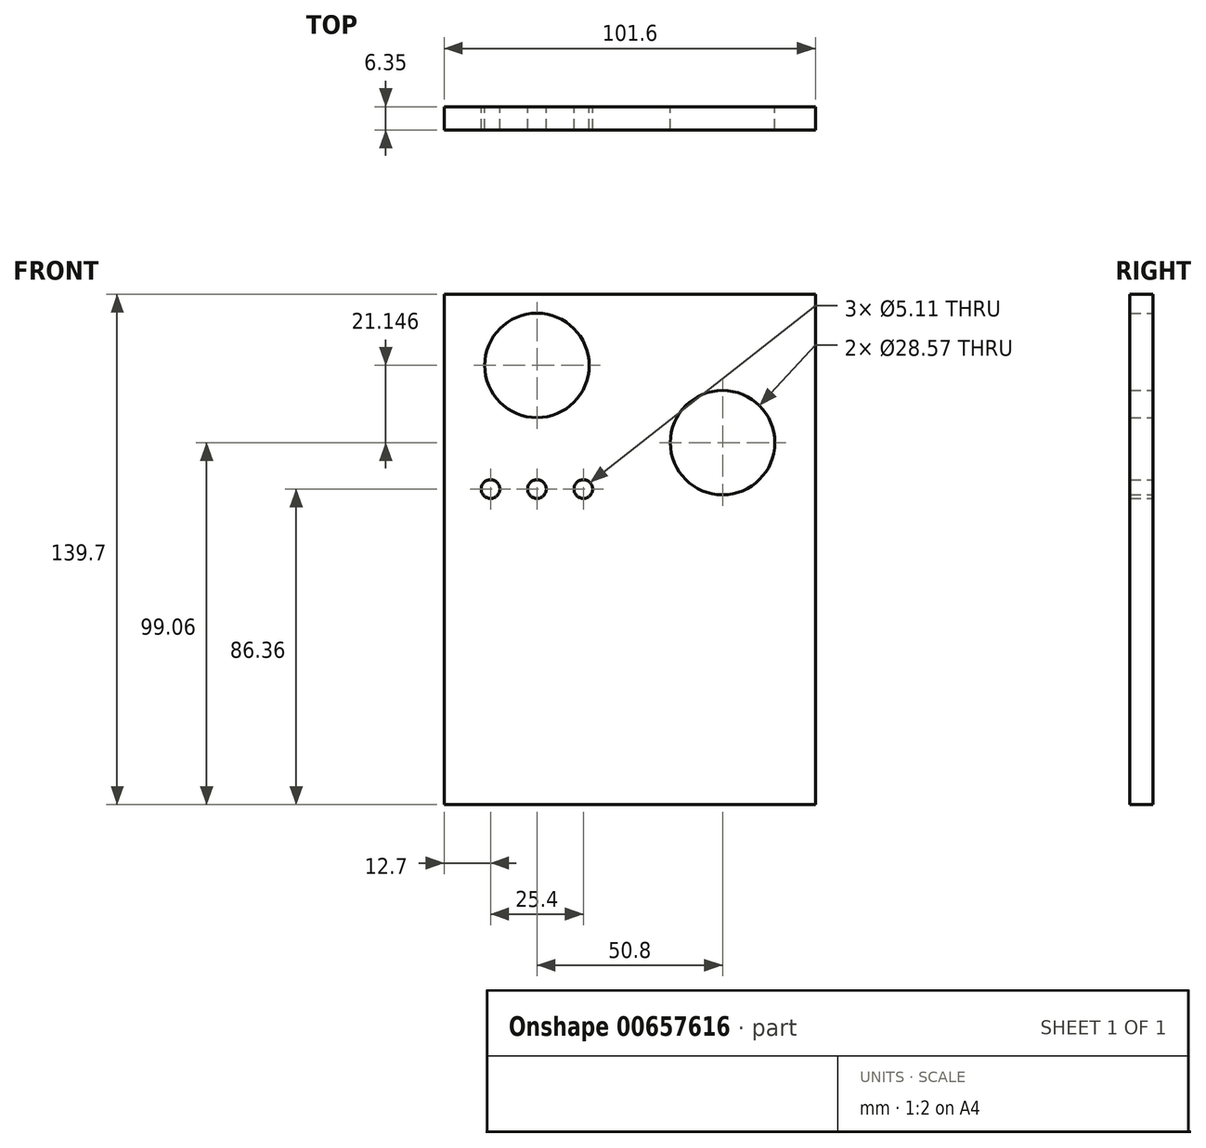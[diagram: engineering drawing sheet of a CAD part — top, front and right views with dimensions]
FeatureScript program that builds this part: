
annotation { "Feature Type Name" : "Feature", "Feature Type Description" : "" }
export const myFeature = defineFeature(function(context is Context, id is Id, definition is map)
    precondition{}
    {
        {
            var Q0;
            Q0=qCreatedBy(makeId("Front.planeOp"),FACE);
            var sketch = newSketch(context, id + "F0", { "sketchPlane" : qUnion([Q0])});
            skLineSegment(sketch, "E0.bottom", {"start": v(0, 0) * mm, "end": v(101.6, 0) * mm});
            skLineSegment(sketch, "E0.top", {"start": v(0, -139.7) * mm, "end": v(101.6, -139.7) * mm});
            skLineSegment(sketch, "E0.left", {"start": v(0, 0) * mm, "end": v(0, -139.7) * mm});
            skLineSegment(sketch, "E0.right", {"start": v(101.6, 0) * mm, "end": v(101.6, -139.7) * mm});
            skCircle(sketch, "E1", {"center": v(12.7, -53.34) * mm, "radius": 2.55 * mm});
            skCircle(sketch, "E2.1.0.0", {"center": v(25.4, -53.34) * mm, "radius": 2.55 * mm});
            skCircle(sketch, "E2.2.0.0", {"center": v(38.1, -53.34) * mm, "radius": 2.55 * mm});
            skLineSegment(sketch, "E2.direction1", {"start": v(12.7, -53.34) * mm, "end": v(25.4, -53.34) * mm, "construction": true});
            skCircle(sketch, "E3", {"center": v(76.2, -40.64) * mm, "radius": 14.29 * mm});
            skCircle(sketch, "E4", {"center": v(25.4, -19.5) * mm, "radius": 14.29 * mm});
            skSolve(sketch);
        }
        {
            var Q0;
            Q0=makeQuery(id+"F0.imprint","IMPRINT",FACE,{"disambiguationData":[TD([[makeQuery(id+"F0.imprint","IMPRINT",EDGE,{"derivedFrom":sQuery(id+"F0.wireOp",EDGE,"E0.bottom")}),-1.0]])]});
            extrude(context, id + "F1", {"entities" : qUnion([Q0]), "depth" : 6.35 * mm, "offsetDistance" : 25.4 * mm});
        }
    });
